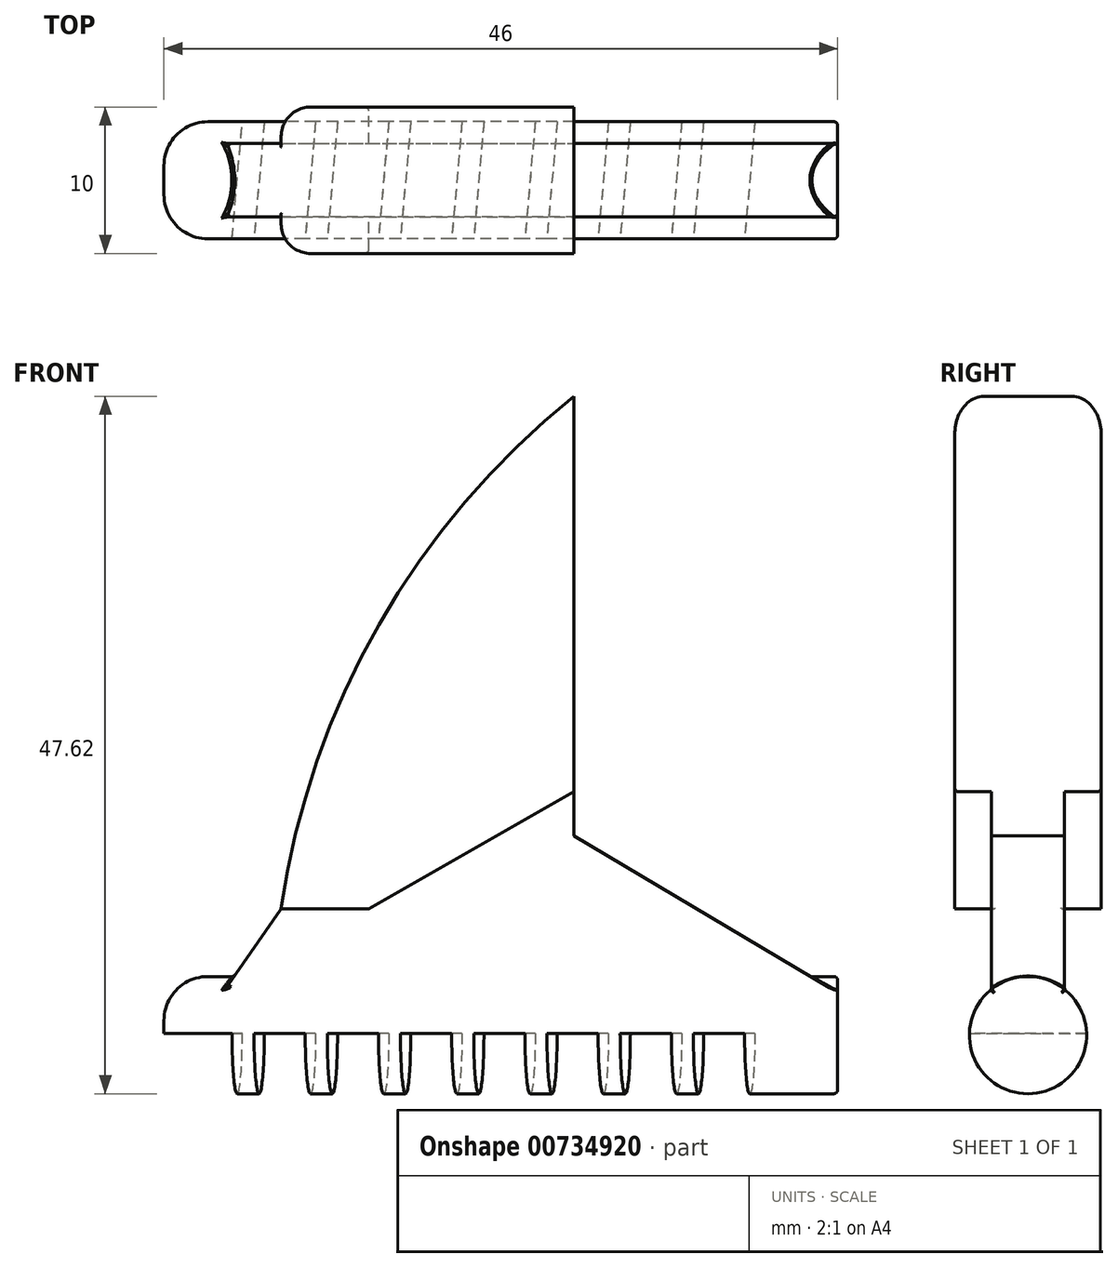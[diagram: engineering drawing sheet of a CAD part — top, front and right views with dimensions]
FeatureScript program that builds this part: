
annotation { "Feature Type Name" : "Feature", "Feature Type Description" : "" }
export const myFeature = defineFeature(function(context is Context, id is Id, definition is map)
    precondition{}
    {
        {
            var Q0;
            Q0=qCreatedBy(makeId("Front.planeOp"),FACE);
            var sketch = newSketch(context, id + "F0", { "sketchPlane" : qUnion([Q0])});
            skLineSegment(sketch, "E0", {"start": v(-20, 0) * mm, "end": v(-14, 0) * mm});
            skLineSegment(sketch, "E1", {"start": v(-14, 0) * mm, "end": v(0, 8) * mm});
            skLineSegment(sketch, "E2", {"start": v(0, 8) * mm, "end": v(0, 35) * mm});
            skArc(sketch, "E3", {"start": v(0, 35) * mm, "mid": v(-13.32, 19.4) * mm, "end": v(-20, 0) * mm});
            skSolve(sketch);
        }
        {
            var Q0;
            Q0 = qSketchRegion(id + "F0", true);
            extrude(context, id + "F1", {"entities" : qUnion([Q0]), "depth" : 10 * mm, "offsetDistance" : 25 * mm, "symmetric" : true});
        }
        {
            var Q0;
            Q0=qCreatedBy(makeId("Front.planeOp"),FACE);
            var sketch = newSketch(context, id + "F2", { "sketchPlane" : qUnion([Q0])});
            skLineSegment(sketch, "E4", {"start": v(0, 8) * mm, "end": v(0, 5) * mm});
            skLineSegment(sketch, "E5", {"start": v(0, 5) * mm, "end": v(17.65, -5.5) * mm});
            skLineSegment(sketch, "E6", {"start": v(17.65, -5.5) * mm, "end": v(-23.85, -5.5) * mm});
            skLineSegment(sketch, "E7", {"start": v(-23.85, -5.5) * mm, "end": v(-20, 0) * mm});
            skLineSegment(sketch, "E8.0", {"start": v(-20, 0) * mm, "end": v(-14, 0) * mm});
            skLineSegment(sketch, "E9.0", {"start": v(-14, 0) * mm, "end": v(0, 8) * mm});
            skSolve(sketch);
        }
        {
            var Q0;
            Q0 = qSketchRegion(id + "F2", true);
            extrude(context, id + "F3", {"entities" : qUnion([Q0]), "operationType" : NewBodyOperationType.ADD, "depth" : 5 * mm, "offsetDistance" : 25 * mm, "symmetric" : true});
        }
        {
            var Q0;
            Q0=qCreatedBy(makeId("Right.planeOp"),FACE);
            var sketch = newSketch(context, id + "F4", { "sketchPlane" : qUnion([Q0])});
            skCircle(sketch, "E10", {"center": v(0, -8.62) * mm, "radius": 4 * mm});
            skSolve(sketch);
        }
        {
            var Q0;
            Q0 = qSketchRegion(id + "F4", true);
            extrude(context, id + "F5", {"entities" : qUnion([Q0]), "operationType" : NewBodyOperationType.ADD, "depth" : 18 * mm, "offsetDistance" : 25 * mm, "hasSecondDirection" : true, "secondDirectionOppositeDirection" : true, "secondDirectionDepth" : 28 * mm});
        }
        {
            var Q0;
            Q0=qCreatedBy(makeId("Top.planeOp"),FACE);
            cPlane(context, id + "F6", {"entities" : qUnion([Q0]), "cplaneType" : CPlaneType.OFFSET, "offset" : 8.5 * mm, "oppositeDirection" : true, "width" : 150 * mm, "height" : 150 * mm});
        }
        {
            var Q0;
            Q0=qCreatedBy(id+"F6.planeOp",FACE);
            var sketch = newSketch(context, id + "F7", { "sketchPlane" : qUnion([Q0])});
            skLineSegment(sketch, "E11", {"start": v(-22.37, 7.2) * mm, "end": v(-23.63, -7.2) * mm, "construction": true});
            skLineSegment(sketch, "E12", {"start": v(-23, 0) * mm, "end": v(-28, 0) * mm, "construction": true});
            skLineSegment(sketch, "E13", {"start": v(-22.56, 5) * mm, "end": v(-26.06, 5) * mm});
            skLineSegment(sketch, "E14", {"start": v(-26.06, 5) * mm, "end": v(-26.94, -5) * mm});
            skLineSegment(sketch, "E15", {"start": v(-26.94, -5) * mm, "end": v(-23.44, -5) * mm});
            skLineSegment(sketch, "E16", {"start": v(-23.44, -5) * mm, "end": v(-22.56, 5) * mm});
            skLineSegment(sketch, "E17.1.0.0", {"start": v(-21.94, -5) * mm, "end": v(-18.44, -5) * mm});
            skLineSegment(sketch, "E17.1.0.1", {"start": v(-21.06, 5) * mm, "end": v(-21.94, -5) * mm});
            skLineSegment(sketch, "E17.1.0.2", {"start": v(-17.56, 5) * mm, "end": v(-21.06, 5) * mm});
            skLineSegment(sketch, "E17.1.0.3", {"start": v(-17.37, 7.2) * mm, "end": v(-18.63, -7.2) * mm, "construction": true});
            skLineSegment(sketch, "E17.2.0.0", {"start": v(-16.94, -5) * mm, "end": v(-13.44, -5) * mm});
            skLineSegment(sketch, "E17.2.0.1", {"start": v(-16.06, 5) * mm, "end": v(-16.94, -5) * mm});
            skLineSegment(sketch, "E17.2.0.2", {"start": v(-12.56, 5) * mm, "end": v(-16.06, 5) * mm});
            skLineSegment(sketch, "E17.2.0.3", {"start": v(-12.37, 7.2) * mm, "end": v(-13.63, -7.2) * mm, "construction": true});
            skLineSegment(sketch, "E17.3.0.0", {"start": v(-11.94, -5) * mm, "end": v(-8.44, -5) * mm});
            skLineSegment(sketch, "E17.3.0.1", {"start": v(-11.06, 5) * mm, "end": v(-11.94, -5) * mm});
            skLineSegment(sketch, "E17.3.0.2", {"start": v(-7.56, 5) * mm, "end": v(-11.06, 5) * mm});
            skLineSegment(sketch, "E17.3.0.3", {"start": v(-7.37, 7.2) * mm, "end": v(-8.63, -7.2) * mm, "construction": true});
            skLineSegment(sketch, "E17.4.0.0", {"start": v(-6.94, -5) * mm, "end": v(-3.44, -5) * mm});
            skLineSegment(sketch, "E17.4.0.1", {"start": v(-6.06, 5) * mm, "end": v(-6.94, -5) * mm});
            skLineSegment(sketch, "E17.4.0.2", {"start": v(-2.56, 5) * mm, "end": v(-6.06, 5) * mm});
            skLineSegment(sketch, "E17.4.0.3", {"start": v(-2.37, 7.2) * mm, "end": v(-3.63, -7.2) * mm, "construction": true});
            skLineSegment(sketch, "E17.5.0.0", {"start": v(-1.94, -5) * mm, "end": v(1.56, -5) * mm});
            skLineSegment(sketch, "E17.5.0.1", {"start": v(-1.06, 5) * mm, "end": v(-1.94, -5) * mm});
            skLineSegment(sketch, "E17.5.0.2", {"start": v(2.44, 5) * mm, "end": v(-1.06, 5) * mm});
            skLineSegment(sketch, "E17.5.0.3", {"start": v(2.63, 7.2) * mm, "end": v(1.37, -7.2) * mm, "construction": true});
            skLineSegment(sketch, "E17.6.0.0", {"start": v(3.06, -5) * mm, "end": v(6.56, -5) * mm});
            skLineSegment(sketch, "E17.6.0.1", {"start": v(3.94, 5) * mm, "end": v(3.06, -5) * mm});
            skLineSegment(sketch, "E17.6.0.2", {"start": v(7.44, 5) * mm, "end": v(3.94, 5) * mm});
            skLineSegment(sketch, "E17.6.0.3", {"start": v(7.63, 7.2) * mm, "end": v(6.37, -7.2) * mm, "construction": true});
            skLineSegment(sketch, "E17.7.0.0", {"start": v(8.06, -5) * mm, "end": v(11.56, -5) * mm});
            skLineSegment(sketch, "E17.7.0.1", {"start": v(8.94, 5) * mm, "end": v(8.06, -5) * mm});
            skLineSegment(sketch, "E17.7.0.2", {"start": v(12.44, 5) * mm, "end": v(8.94, 5) * mm});
            skLineSegment(sketch, "E17.7.0.3", {"start": v(12.63, 7.2) * mm, "end": v(11.37, -7.2) * mm, "construction": true});
            skLineSegment(sketch, "E17.direction1", {"start": v(-26.94, -5) * mm, "end": v(-21.94, -5) * mm, "construction": true});
            skLineSegment(sketch, "E18", {"start": v(-17.56, 5) * mm, "end": v(-18.44, -5) * mm});
            skLineSegment(sketch, "E19", {"start": v(-12.56, 5) * mm, "end": v(-13.44, -5) * mm});
            skLineSegment(sketch, "E20", {"start": v(-7.56, 5) * mm, "end": v(-8.44, -5) * mm});
            skLineSegment(sketch, "E21", {"start": v(-2.56, 5) * mm, "end": v(-3.44, -5) * mm});
            skLineSegment(sketch, "E22", {"start": v(2.44, 5) * mm, "end": v(1.56, -5) * mm});
            skLineSegment(sketch, "E23", {"start": v(7.44, 5) * mm, "end": v(6.56, -5) * mm});
            skLineSegment(sketch, "E24", {"start": v(12.44, 5) * mm, "end": v(11.56, -5) * mm});
            skSolve(sketch);
        }
        {
            var Q0;
            Q0 = qSketchRegion(id + "F7", true);
            extrude(context, id + "F8", {"entities" : qUnion([Q0]), "operationType" : NewBodyOperationType.REMOVE, "endBound" : BoundingType.THROUGH_ALL, "oppositeDirection" : true, "depth" : 25 * mm, "offsetDistance" : 25 * mm});
        }
        {
            var Q0;
            Q0=makeQuery(id+"F8.boolean.opBoolean","COPY",FACE,{"derivedFrom":makeQuery(id+"F8.opExtrude","CAP_FACE",FACE,{"disambiguationData":[OSD([sQuery(id+"F7.wireOp",EDGE,"E13"),sQuery(id+"F7.wireOp",EDGE,"E14"),sQuery(id+"F7.wireOp",EDGE,"E15"),sQuery(id+"F7.wireOp",EDGE,"E16")])],"isStart":true})});
            var sketch = newSketch(context, id + "F9", { "sketchPlane" : qUnion([Q0])});
            skLineSegment(sketch, "E25", {"start": v(-25.1, 6.54) * mm, "end": v(-25.1, -6.4) * mm, "construction": true});
            skPoint(sketch, "E25.startSnap0", {"position": v(-25.1, 4) * mm});
            skLineSegment(sketch, "E26.bottom", {"start": v(-25.1, 6.54) * mm, "end": v(-34.06, 6.54) * mm});
            skLineSegment(sketch, "E26.top", {"start": v(-25.1, -6.4) * mm, "end": v(-34.06, -6.4) * mm});
            skLineSegment(sketch, "E26.left", {"start": v(-25.1, 6.54) * mm, "end": v(-25.1, -6.4) * mm});
            skLineSegment(sketch, "E26.right", {"start": v(-34.06, 6.54) * mm, "end": v(-34.06, -6.4) * mm});
            skSolve(sketch);
        }
        {
            var Q0;
            Q0 = qSketchRegion(id + "F9", true);
            extrude(context, id + "F10", {"entities" : qUnion([Q0]), "operationType" : NewBodyOperationType.REMOVE, "endBound" : BoundingType.THROUGH_ALL, "depth" : 25 * mm, "offsetDistance" : 25 * mm});
        }
        {
            var Q0;
            Q0=makeQuery(id+"F5.opExtrude","CAP_EDGE",EDGE,{"disambiguationData":[OSD([sQuery(id+"F4.wireOp",EDGE,"E10")])],"isStart":true});
            fillet(context, id + "F11", {"entities" : qUnion([Q0]), "radius" : 3 * mm, "tangentPropagation" : true, "allowEdgeOverflow" : false});
        }
        {
            var Q0;
            Q0=makeQuery(id+"F3.opExtrude","CAP_EDGE",EDGE,{"disambiguationData":[OSD([sQuery(id+"F2.wireOp",EDGE,"E8.0")])],"isStart":false});
            var Q1;
            Q1=makeQuery(id+"F3.opExtrude","CAP_EDGE",EDGE,{"disambiguationData":[OSD([sQuery(id+"F2.wireOp",EDGE,"E9.0")])],"isStart":false});
            var Q2;
            Q2=makeQuery(id+"F5.boolean.opBoolean","INTERSECT",EDGE,{"derivedFrom":[makeQuery(id+"F3.opExtrude","CAP_FACE",FACE,{"disambiguationData":[OSD([sQuery(id+"F2.wireOp",EDGE,"E4"),sQuery(id+"F2.wireOp",EDGE,"E5"),sQuery(id+"F2.wireOp",EDGE,"E6"),sQuery(id+"F2.wireOp",EDGE,"E7"),sQuery(id+"F2.wireOp",EDGE,"E8.0"),sQuery(id+"F2.wireOp",EDGE,"E9.0")])],"isStart":false}),makeQuery(id+"F5.opExtrude","SWEPT_FACE",FACE,{"disambiguationData":[OSD([sQuery(id+"F4.wireOp",EDGE,"E10")])]})]});
            var Q3;
            Q3=makeQuery(id+"F5.boolean.opBoolean","INTERSECT",EDGE,{"derivedFrom":[makeQuery(id+"F3.opExtrude","CAP_FACE",FACE,{"disambiguationData":[OSD([sQuery(id+"F2.wireOp",EDGE,"E4"),sQuery(id+"F2.wireOp",EDGE,"E5"),sQuery(id+"F2.wireOp",EDGE,"E6"),sQuery(id+"F2.wireOp",EDGE,"E7"),sQuery(id+"F2.wireOp",EDGE,"E8.0"),sQuery(id+"F2.wireOp",EDGE,"E9.0")])],"isStart":true}),makeQuery(id+"F5.opExtrude","SWEPT_FACE",FACE,{"disambiguationData":[OSD([sQuery(id+"F4.wireOp",EDGE,"E10")])]})]});
            var Q4;
            Q4=makeQuery(id+"F3.opExtrude","CAP_EDGE",EDGE,{"disambiguationData":[OSD([sQuery(id+"F2.wireOp",EDGE,"E9.0")])],"isStart":true});
            var Q5;
            Q5=makeQuery(id+"F3.opExtrude","CAP_EDGE",EDGE,{"disambiguationData":[OSD([sQuery(id+"F2.wireOp",EDGE,"E8.0")])],"isStart":true});
            var Q6;
            Q6=makeQuery(id+"F3.boolean.opBoolean","MERGE",EDGE,{"derivedFrom":[makeQuery(id+"F1.opExtrude","SWEPT_EDGE",EDGE,{"disambiguationData":[OSD([sQuery(id+"F0.wireOp",EDGE,"E0"),sQuery(id+"F0.wireOp",EDGE,"E3")])]}),makeQuery(id+"F3.opExtrude","SWEPT_EDGE",EDGE,{"disambiguationData":[OSD([sQuery(id+"F2.wireOp",EDGE,"E7"),sQuery(id+"F2.wireOp",EDGE,"E8.0")])]})]});
            var Q7;
            Q7=makeQuery(id+"F5.boolean.opBoolean","INTERSECT",EDGE,{"derivedFrom":[makeQuery(id+"F3.opExtrude","SWEPT_FACE",FACE,{"disambiguationData":[OSD([sQuery(id+"F2.wireOp",EDGE,"E5")])]}),makeQuery(id+"F5.opExtrude","SWEPT_FACE",FACE,{"disambiguationData":[OSD([sQuery(id+"F4.wireOp",EDGE,"E10")])]})]});
            var Q8;
            Q8=makeQuery(id+"F5.boolean.opBoolean","INTERSECT",EDGE,{"derivedFrom":[makeQuery(id+"F3.opExtrude","SWEPT_FACE",FACE,{"disambiguationData":[OSD([sQuery(id+"F2.wireOp",EDGE,"E7")])]}),makeQuery(id+"F5.opExtrude","SWEPT_FACE",FACE,{"disambiguationData":[OSD([sQuery(id+"F4.wireOp",EDGE,"E10")])]})]});
            fillet(context, id + "F12", {"entities" : qUnion([Q0, Q1, Q2, Q3, Q4, Q5, Q6, Q7, Q8]), "radius" : 0.25 * mm, "tangentPropagation" : true, "allowEdgeOverflow" : false});
        }
        {
            var Q0;
            Q0=makeQuery(id+"F1.opExtrude","CAP_EDGE",EDGE,{"disambiguationData":[OSD([sQuery(id+"F0.wireOp",EDGE,"E3")])],"isStart":false});
            var Q1;
            Q1=makeQuery(id+"F1.opExtrude","CAP_EDGE",EDGE,{"disambiguationData":[OSD([sQuery(id+"F0.wireOp",EDGE,"E3")])],"isStart":true});
            fillet(context, id + "F13", {"entities" : qUnion([Q0, Q1]), "radius" : 2 * mm, "tangentPropagation" : true, "allowEdgeOverflow" : false});
        }
        {
            var Q0;
            Q0=makeQuery(id+"F3.opExtrude","SWEPT_FACE",FACE,{"disambiguationData":[OSD([sQuery(id+"F2.wireOp",EDGE,"E7")])]});
            var Q1;
            Q1=makeQuery(id+"F1.opExtrude","CAP_EDGE",EDGE,{"disambiguationData":[OSD([sQuery(id+"F0.wireOp",EDGE,"E1")])],"isStart":false});
            var Q2;
            Q2=makeQuery(id+"F1.opExtrude","CAP_EDGE",EDGE,{"disambiguationData":[OSD([sQuery(id+"F0.wireOp",EDGE,"E1")])],"isStart":true});
            var Q3;
            Q3=makeQuery(id+"F5.opExtrude","CAP_EDGE",EDGE,{"disambiguationData":[OSD([sQuery(id+"F4.wireOp",EDGE,"E10")])],"isStart":false});
            fillet(context, id + "F14", {"entities" : qUnion([Q0, Q1, Q2, Q3]), "radius" : 0.25 * mm, "tangentPropagation" : true, "allowEdgeOverflow" : false});
        }
    });
